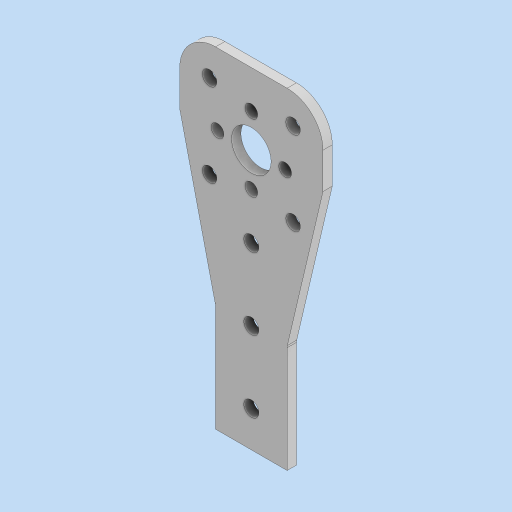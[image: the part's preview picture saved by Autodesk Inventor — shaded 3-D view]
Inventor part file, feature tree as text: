
AUTODESK INVENTOR PART (.ipt)
format: ipt  version: 2024 (Build 280153000, 153)  size: 162,816 bytes
history: native  units: in
note: dims shown in document units (in); Inventor stores cm internally (conversion verified against a paired STEP export)
features: fillet x3, extrude x1, sketch x1
ambient origin geometry x8: Origin, YZ Plane, XZ Plane, XY Plane, X Axis, Y Axis, Z Axis, Center Point
bodies: Solid1 (feature_tree)
feature tree (5):
  extrude  "Extrusion1"  Depth=0.5in
  fillet  "Fillet13"  Radius=0.209in
  fillet  "Fillet14"  Radius=0.875in
  fillet  "Fillet15"  Radius=0.13in
  sketch  "Sketch1"  dims[d2=0.5512in d3=0.209in d4=0.209in d5=0.875in d10=0.13in d11=0.0in d24=0.125in d25=0.125in d26=1.0in d27=1.5in d28=1.0in d29=1.125in d30=2.125in d31=0.177in d32=0.4724in d33=0.4724in d34=0.4724in d35=0.4724in d36=1.65in d37=0.201in d38=0.583in d39=1.5748in d41=360.0deg d43=2.0in d44=0.0in d45=1.0in d46=1.0in d47=1.0in d48=0.5in d16=0.0in d17=0.0in d18=0.0in d19=0.0in d20=0.0in d21=0.0in d22=0.0in d23=0.0in]
